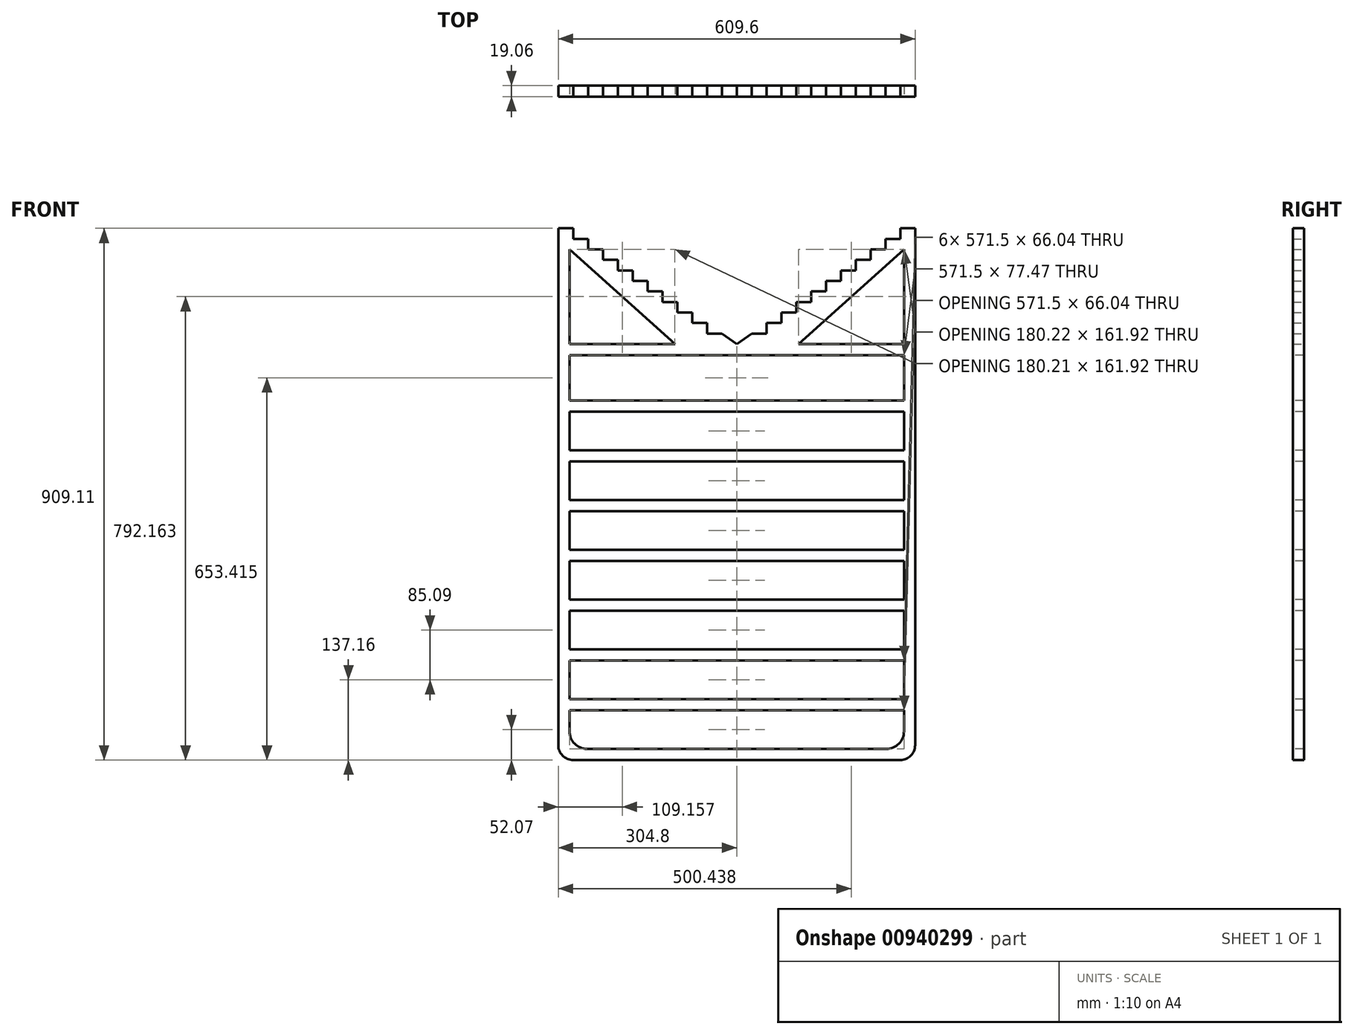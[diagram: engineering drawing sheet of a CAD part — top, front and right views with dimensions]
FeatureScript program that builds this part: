
annotation { "Feature Type Name" : "Feature", "Feature Type Description" : "" }
export const myFeature = defineFeature(function(context is Context, id is Id, definition is map)
    precondition{}
    {
        {
            var Q0;
            Q0=qCreatedBy(makeId("Front.planeOp"),FACE);
            var sketch = newSketch(context, id + "F0", { "sketchPlane" : qUnion([Q0])});
            skLineSegment(sketch, "E0.bottom", {"start": v(-304.8, -355.6) * mm, "end": v(304.8, -355.6) * mm});
            skLineSegment(sketch, "E0.top", {"start": v(-304.8, 355.6) * mm, "end": v(304.8, 355.6) * mm});
            skLineSegment(sketch, "E0.left", {"start": v(-304.8, -355.6) * mm, "end": v(-304.8, 355.6) * mm});
            skLineSegment(sketch, "E0.right", {"start": v(304.8, -355.6) * mm, "end": v(304.8, 355.6) * mm});
            skPoint(sketch, "E0.middle", {"position": v(0, 0) * mm});
            skLineSegment(sketch, "E1", {"start": v(-304.8, 355.6) * mm, "end": v(-304.8, 571.5) * mm});
            skLineSegment(sketch, "E2", {"start": v(304.8, 355.6) * mm, "end": v(304.8, 571.5) * mm});
            skLineSegment(sketch, "E3", {"start": v(304.8, 571.5) * mm, "end": v(304.8, 571.5) * mm});
            skLineSegment(sketch, "E4", {"start": v(304.8, 571.5) * mm, "end": v(0, 355.6) * mm});
            skLineSegment(sketch, "E5", {"start": v(0, 355.6) * mm, "end": v(-304.8, 571.5) * mm});
            skLineSegment(sketch, "E6", {"start": v(-304.8, 571.5) * mm, "end": v(-304.8, 571.5) * mm});
            skLineSegment(sketch, "E7.bottom", {"start": v(-279.4, 571.5) * mm, "end": v(-304.8, 571.5) * mm});
            skLineSegment(sketch, "E7.top", {"start": v(-279.4, 553.5) * mm, "end": v(-304.8, 553.5) * mm});
            skLineSegment(sketch, "E7.left", {"start": v(-279.4, 571.5) * mm, "end": v(-279.4, 553.5) * mm});
            skLineSegment(sketch, "E7.right", {"start": v(-304.8, 571.5) * mm, "end": v(-304.8, 553.5) * mm});
            skPoint(sketch, "E7.middle", {"position": v(-292.1, 562.5) * mm});
            skLineSegment(sketch, "E8.bottom", {"start": v(279.4, 571.5) * mm, "end": v(304.8, 571.5) * mm});
            skLineSegment(sketch, "E8.top", {"start": v(279.4, 553.5) * mm, "end": v(304.8, 553.5) * mm});
            skLineSegment(sketch, "E8.left", {"start": v(279.4, 571.5) * mm, "end": v(279.4, 553.5) * mm});
            skLineSegment(sketch, "E8.right", {"start": v(304.8, 571.5) * mm, "end": v(304.8, 553.5) * mm});
            skPoint(sketch, "E8.middle", {"position": v(292.1, 562.5) * mm});
            skLineSegment(sketch, "E9.bottom", {"start": v(-279.4, 553.5) * mm, "end": v(-254, 553.5) * mm});
            skLineSegment(sketch, "E9.top", {"start": v(-279.4, 535.52) * mm, "end": v(-254, 535.52) * mm});
            skLineSegment(sketch, "E9.left", {"start": v(-279.4, 553.5) * mm, "end": v(-279.4, 535.52) * mm});
            skLineSegment(sketch, "E9.right", {"start": v(-254, 553.5) * mm, "end": v(-254, 535.52) * mm});
            skLineSegment(sketch, "E10.bottom", {"start": v(-254, 535.52) * mm, "end": v(-228.6, 535.52) * mm});
            skLineSegment(sketch, "E10.top", {"start": v(-254, 517.52) * mm, "end": v(-228.6, 517.52) * mm});
            skLineSegment(sketch, "E10.left", {"start": v(-254, 535.52) * mm, "end": v(-254, 517.52) * mm});
            skLineSegment(sketch, "E10.right", {"start": v(-228.6, 535.52) * mm, "end": v(-228.6, 517.52) * mm});
            skLineSegment(sketch, "E11.bottom", {"start": v(-228.6, 517.52) * mm, "end": v(-203.2, 517.52) * mm});
            skLineSegment(sketch, "E11.top", {"start": v(-228.6, 499.53) * mm, "end": v(-203.2, 499.53) * mm});
            skLineSegment(sketch, "E11.left", {"start": v(-228.6, 517.52) * mm, "end": v(-228.6, 499.53) * mm});
            skLineSegment(sketch, "E11.right", {"start": v(-203.2, 517.52) * mm, "end": v(-203.2, 499.53) * mm});
            skLineSegment(sketch, "E12.bottom", {"start": v(-203.2, 499.53) * mm, "end": v(-177.8, 499.53) * mm});
            skLineSegment(sketch, "E12.top", {"start": v(-203.2, 481.54) * mm, "end": v(-177.8, 481.54) * mm});
            skLineSegment(sketch, "E12.left", {"start": v(-203.2, 499.53) * mm, "end": v(-203.2, 481.54) * mm});
            skLineSegment(sketch, "E12.right", {"start": v(-177.8, 499.53) * mm, "end": v(-177.8, 481.54) * mm});
            skLineSegment(sketch, "E13.bottom", {"start": v(279.4, 553.5) * mm, "end": v(254, 553.5) * mm});
            skLineSegment(sketch, "E13.top", {"start": v(279.4, 535.52) * mm, "end": v(254, 535.52) * mm});
            skLineSegment(sketch, "E13.left", {"start": v(279.4, 553.5) * mm, "end": v(279.4, 535.52) * mm});
            skLineSegment(sketch, "E13.right", {"start": v(254, 553.5) * mm, "end": v(254, 535.52) * mm});
            skLineSegment(sketch, "E14.bottom", {"start": v(254, 535.52) * mm, "end": v(228.6, 535.52) * mm});
            skLineSegment(sketch, "E14.top", {"start": v(254, 517.52) * mm, "end": v(228.6, 517.52) * mm});
            skLineSegment(sketch, "E14.left", {"start": v(254, 535.52) * mm, "end": v(254, 517.52) * mm});
            skLineSegment(sketch, "E14.right", {"start": v(228.6, 535.52) * mm, "end": v(228.6, 517.52) * mm});
            skLineSegment(sketch, "E15.bottom", {"start": v(-177.8, 481.54) * mm, "end": v(-152.4, 481.54) * mm});
            skLineSegment(sketch, "E15.top", {"start": v(-177.8, 463.55) * mm, "end": v(-152.4, 463.55) * mm});
            skLineSegment(sketch, "E15.left", {"start": v(-177.8, 481.54) * mm, "end": v(-177.8, 463.55) * mm});
            skLineSegment(sketch, "E15.right", {"start": v(-152.4, 481.54) * mm, "end": v(-152.4, 463.55) * mm});
            skLineSegment(sketch, "E16.bottom", {"start": v(-152.4, 463.55) * mm, "end": v(-127, 463.55) * mm});
            skLineSegment(sketch, "E16.top", {"start": v(-152.4, 445.56) * mm, "end": v(-127, 445.56) * mm});
            skLineSegment(sketch, "E16.left", {"start": v(-152.4, 463.55) * mm, "end": v(-152.4, 445.56) * mm});
            skLineSegment(sketch, "E16.right", {"start": v(-127, 463.55) * mm, "end": v(-127, 445.56) * mm});
            skLineSegment(sketch, "E17.bottom", {"start": v(-127, 445.56) * mm, "end": v(-101.6, 445.56) * mm});
            skLineSegment(sketch, "E17.top", {"start": v(-127, 427.57) * mm, "end": v(-101.6, 427.57) * mm});
            skLineSegment(sketch, "E17.left", {"start": v(-127, 445.56) * mm, "end": v(-127, 427.57) * mm});
            skLineSegment(sketch, "E17.right", {"start": v(-101.6, 445.56) * mm, "end": v(-101.6, 427.57) * mm});
            skLineSegment(sketch, "E18.bottom", {"start": v(-101.6, 427.57) * mm, "end": v(-76.2, 427.57) * mm});
            skLineSegment(sketch, "E18.top", {"start": v(-101.6, 409.57) * mm, "end": v(-76.2, 409.57) * mm});
            skLineSegment(sketch, "E18.left", {"start": v(-101.6, 427.57) * mm, "end": v(-101.6, 409.57) * mm});
            skLineSegment(sketch, "E18.right", {"start": v(-76.2, 427.57) * mm, "end": v(-76.2, 409.57) * mm});
            skLineSegment(sketch, "E19.bottom", {"start": v(-76.2, 409.57) * mm, "end": v(-50.8, 409.57) * mm});
            skLineSegment(sketch, "E19.top", {"start": v(-76.2, 391.58) * mm, "end": v(-50.8, 391.58) * mm});
            skLineSegment(sketch, "E19.left", {"start": v(-76.2, 409.57) * mm, "end": v(-76.2, 391.58) * mm});
            skLineSegment(sketch, "E19.right", {"start": v(-50.8, 409.57) * mm, "end": v(-50.8, 391.58) * mm});
            skLineSegment(sketch, "E20.bottom", {"start": v(-50.8, 391.58) * mm, "end": v(-25.4, 391.58) * mm});
            skLineSegment(sketch, "E20.top", {"start": v(-50.8, 373.6) * mm, "end": v(-25.4, 373.6) * mm});
            skLineSegment(sketch, "E20.left", {"start": v(-50.8, 391.58) * mm, "end": v(-50.8, 373.6) * mm});
            skLineSegment(sketch, "E20.right", {"start": v(-25.4, 391.58) * mm, "end": v(-25.4, 373.6) * mm});
            skPoint(sketch, "E21.right.start.orphan", {"position": v(203.2, 499.53) * mm});
            skPoint(sketch, "E22.top.end.orphan", {"position": v(177.8, 481.54) * mm});
            skLineSegment(sketch, "E23.bottom", {"start": v(228.6, 517.52) * mm, "end": v(203.2, 517.52) * mm});
            skLineSegment(sketch, "E23.top", {"start": v(228.6, 499.53) * mm, "end": v(203.2, 499.53) * mm});
            skLineSegment(sketch, "E23.left", {"start": v(228.6, 517.52) * mm, "end": v(228.6, 499.53) * mm});
            skLineSegment(sketch, "E23.right", {"start": v(203.2, 517.52) * mm, "end": v(203.2, 499.53) * mm});
            skLineSegment(sketch, "E24.bottom", {"start": v(203.2, 499.53) * mm, "end": v(177.8, 499.53) * mm});
            skLineSegment(sketch, "E24.top", {"start": v(203.2, 481.54) * mm, "end": v(177.8, 481.54) * mm});
            skLineSegment(sketch, "E24.left", {"start": v(203.2, 499.53) * mm, "end": v(203.2, 481.54) * mm});
            skLineSegment(sketch, "E24.right", {"start": v(177.8, 499.53) * mm, "end": v(177.8, 481.54) * mm});
            skLineSegment(sketch, "E25.bottom", {"start": v(177.8, 481.54) * mm, "end": v(152.4, 481.54) * mm});
            skLineSegment(sketch, "E25.top", {"start": v(177.8, 463.55) * mm, "end": v(152.4, 463.55) * mm});
            skLineSegment(sketch, "E25.left", {"start": v(177.8, 481.54) * mm, "end": v(177.8, 463.55) * mm});
            skLineSegment(sketch, "E25.right", {"start": v(152.4, 481.54) * mm, "end": v(152.4, 463.55) * mm});
            skLineSegment(sketch, "E26.bottom", {"start": v(152.4, 463.55) * mm, "end": v(127, 463.55) * mm});
            skLineSegment(sketch, "E26.top", {"start": v(152.4, 445.56) * mm, "end": v(127, 445.56) * mm});
            skLineSegment(sketch, "E26.left", {"start": v(152.4, 463.55) * mm, "end": v(152.4, 445.56) * mm});
            skLineSegment(sketch, "E26.right", {"start": v(127, 463.55) * mm, "end": v(127, 445.56) * mm});
            skLineSegment(sketch, "E27.bottom", {"start": v(127, 445.56) * mm, "end": v(101.6, 445.56) * mm});
            skLineSegment(sketch, "E27.top", {"start": v(127, 427.57) * mm, "end": v(101.6, 427.57) * mm});
            skLineSegment(sketch, "E27.left", {"start": v(127, 445.56) * mm, "end": v(127, 427.57) * mm});
            skLineSegment(sketch, "E27.right", {"start": v(101.6, 445.56) * mm, "end": v(101.6, 427.57) * mm});
            skLineSegment(sketch, "E28.bottom", {"start": v(101.6, 427.57) * mm, "end": v(76.2, 427.57) * mm});
            skLineSegment(sketch, "E28.top", {"start": v(101.6, 409.57) * mm, "end": v(76.2, 409.57) * mm});
            skLineSegment(sketch, "E28.left", {"start": v(101.6, 427.57) * mm, "end": v(101.6, 409.57) * mm});
            skLineSegment(sketch, "E28.right", {"start": v(76.2, 427.57) * mm, "end": v(76.2, 409.57) * mm});
            skLineSegment(sketch, "E29.bottom", {"start": v(76.2, 409.57) * mm, "end": v(50.8, 409.57) * mm});
            skLineSegment(sketch, "E29.top", {"start": v(76.2, 391.58) * mm, "end": v(50.8, 391.58) * mm});
            skLineSegment(sketch, "E29.left", {"start": v(76.2, 409.57) * mm, "end": v(76.2, 391.58) * mm});
            skLineSegment(sketch, "E29.right", {"start": v(50.8, 409.57) * mm, "end": v(50.8, 391.58) * mm});
            skLineSegment(sketch, "E30.bottom", {"start": v(50.8, 391.58) * mm, "end": v(25.4, 391.58) * mm});
            skLineSegment(sketch, "E30.top", {"start": v(50.8, 373.6) * mm, "end": v(25.4, 373.6) * mm});
            skLineSegment(sketch, "E30.left", {"start": v(50.8, 391.58) * mm, "end": v(50.8, 373.6) * mm});
            skLineSegment(sketch, "E30.right", {"start": v(25.4, 391.58) * mm, "end": v(25.4, 373.6) * mm});
            skSolve(sketch);
        }
        {
            var Q0;
            Q0=makeQuery(id+"F0.imprint","IMPRINT",FACE,{"disambiguationData":[TD([[makeQuery(id+"F0.imprint","IMPRINT",EDGE,{"derivedFrom":sQuery(id+"F0.wireOp",EDGE,"E0.bottom")}),1.0]])]});
            var Q1;
            {var subQ0=sQuery(id+"F0.wireOp",EDGE,"E7.top");Q1=makeQuery(id+"F0.imprint","IMPRINT",FACE,{"disambiguationData":[TD([[makeQuery(id+"F0.imprint","IMPRINT",EDGE,{"derivedFrom":subQ0}),1.0]])]});}
            var Q2;
            {var subQ3=sQuery(id+"F0.wireOp",EDGE,"E8.top");Q2=makeQuery(id+"F0.imprint","IMPRINT",FACE,{"disambiguationData":[TD([[makeQuery(id+"F0.imprint","IMPRINT",EDGE,{"derivedFrom":subQ3}),-1.0]])]});}
            extrude(context, id + "F1", {"entities" : qUnion([Q0, Q1, Q2]), "endBound" : BoundingType.SYMMETRIC, "depth" : 19.05 * mm, "offsetDistance" : 25.4 * mm});
        }
        {
            var Q0;
            Q0=makeQuery(id+"F1.opExtrude","SWEPT_EDGE",EDGE,{"disambiguationData":[OSD([sQuery(id+"F0.wireOp",EDGE,"E0.bottom"),sQuery(id+"F0.wireOp",EDGE,"E0.left")])]});
            var Q1;
            Q1=makeQuery(id+"F1.opExtrude","SWEPT_EDGE",EDGE,{"disambiguationData":[OSD([sQuery(id+"F0.wireOp",EDGE,"E0.bottom"),sQuery(id+"F0.wireOp",EDGE,"E0.right")])]});
            fillet(context, id + "F2", {"entities" : qUnion([Q0, Q1]), "radius" : 25.4 * mm, "tangentPropagation" : true, "allowEdgeOverflow" : false});
        }
        {
            var Q0;
            Q0=makeQuery(id+"F1.opExtrude","CAP_FACE",FACE,{"disambiguationData":[OSD([sQuery(id+"F0.wireOp",EDGE,"E0.bottom"),sQuery(id+"F0.wireOp",EDGE,"E0.left"),sQuery(id+"F0.wireOp",EDGE,"E0.right"),sQuery(id+"F0.wireOp",EDGE,"E1"),sQuery(id+"F0.wireOp",EDGE,"E2"),sQuery(id+"F0.wireOp",EDGE,"E4"),sQuery(id+"F0.wireOp",EDGE,"E5"),sQuery(id+"F0.wireOp",EDGE,"E7.top"),sQuery(id+"F0.wireOp",EDGE,"E8.top"),sQuery(id+"F0.wireOp",EDGE,"E9.top"),sQuery(id+"F0.wireOp",EDGE,"E9.left"),sQuery(id+"F0.wireOp",EDGE,"E10.top"),sQuery(id+"F0.wireOp",EDGE,"E10.left"),sQuery(id+"F0.wireOp",EDGE,"E11.top"),sQuery(id+"F0.wireOp",EDGE,"E11.left"),sQuery(id+"F0.wireOp",EDGE,"E12.top"),sQuery(id+"F0.wireOp",EDGE,"E12.left"),sQuery(id+"F0.wireOp",EDGE,"E13.top"),sQuery(id+"F0.wireOp",EDGE,"E13.left"),sQuery(id+"F0.wireOp",EDGE,"E14.top"),sQuery(id+"F0.wireOp",EDGE,"E14.left"),sQuery(id+"F0.wireOp",EDGE,"E15.top"),sQuery(id+"F0.wireOp",EDGE,"E15.left"),sQuery(id+"F0.wireOp",EDGE,"E16.top"),sQuery(id+"F0.wireOp",EDGE,"E16.left"),sQuery(id+"F0.wireOp",EDGE,"E17.top"),sQuery(id+"F0.wireOp",EDGE,"E17.left"),sQuery(id+"F0.wireOp",EDGE,"E18.top"),sQuery(id+"F0.wireOp",EDGE,"E18.left"),sQuery(id+"F0.wireOp",EDGE,"E19.top"),sQuery(id+"F0.wireOp",EDGE,"E19.left"),sQuery(id+"F0.wireOp",EDGE,"E20.top"),sQuery(id+"F0.wireOp",EDGE,"E20.left"),sQuery(id+"F0.wireOp",EDGE,"E23.top"),sQuery(id+"F0.wireOp",EDGE,"E23.left"),sQuery(id+"F0.wireOp",EDGE,"E24.top"),sQuery(id+"F0.wireOp",EDGE,"E24.left"),sQuery(id+"F0.wireOp",EDGE,"E25.top"),sQuery(id+"F0.wireOp",EDGE,"E25.left"),sQuery(id+"F0.wireOp",EDGE,"E26.top"),sQuery(id+"F0.wireOp",EDGE,"E26.left"),sQuery(id+"F0.wireOp",EDGE,"E27.top"),sQuery(id+"F0.wireOp",EDGE,"E27.left"),sQuery(id+"F0.wireOp",EDGE,"E28.top"),sQuery(id+"F0.wireOp",EDGE,"E28.left"),sQuery(id+"F0.wireOp",EDGE,"E29.top"),sQuery(id+"F0.wireOp",EDGE,"E29.left"),sQuery(id+"F0.wireOp",EDGE,"E30.top"),sQuery(id+"F0.wireOp",EDGE,"E30.left")])],"isStart":false});
            var sketch = newSketch(context, id + "F3", { "sketchPlane" : qUnion([Q0])});
            skLineSegment(sketch, "E31.bottom", {"start": v(-285.75, -336.55) * mm, "end": v(285.75, -336.55) * mm});
            skLineSegment(sketch, "E31.top", {"start": v(-285.75, 336.55) * mm, "end": v(285.75, 336.55) * mm});
            skLineSegment(sketch, "E31.left", {"start": v(-285.75, -336.55) * mm, "end": v(-285.75, 336.55) * mm});
            skLineSegment(sketch, "E31.right", {"start": v(285.75, -336.55) * mm, "end": v(285.75, 336.55) * mm});
            skPoint(sketch, "E31.middle", {"position": v(0, 0) * mm});
            skSolve(sketch);
        }
        {
            var Q0;
            Q0 = qSketchRegion(id + "F3", true);
            extrude(context, id + "F4", {"entities" : qUnion([Q0]), "operationType" : NewBodyOperationType.REMOVE, "endBound" : BoundingType.THROUGH_ALL, "oppositeDirection" : true, "depth" : 25.4 * mm, "offsetDistance" : 25.4 * mm});
        }
        {
            var Q0;
            Q0=makeQuery(id+"F4.boolean.opBoolean","COPY",EDGE,{"derivedFrom":makeQuery(id+"F4.opExtrude","SWEPT_EDGE",EDGE,{"disambiguationData":[OSD([sQuery(id+"F3.wireOp",EDGE,"E31.bottom"),sQuery(id+"F3.wireOp",EDGE,"E31.right")])]})});
            var Q1;
            Q1=makeQuery(id+"F4.boolean.opBoolean","COPY",EDGE,{"derivedFrom":makeQuery(id+"F4.opExtrude","SWEPT_EDGE",EDGE,{"disambiguationData":[OSD([sQuery(id+"F3.wireOp",EDGE,"E31.bottom"),sQuery(id+"F3.wireOp",EDGE,"E31.left")])]})});
            fillet(context, id + "F5", {"entities" : qUnion([Q0, Q1]), "radius" : 30.1 * mm, "tangentPropagation" : true, "allowEdgeOverflow" : false});
        }
        {
            var Q0;
            Q0=makeQuery(id+"F1.opExtrude","CAP_FACE",FACE,{"disambiguationData":[OSD([sQuery(id+"F0.wireOp",EDGE,"E0.bottom"),sQuery(id+"F0.wireOp",EDGE,"E0.left"),sQuery(id+"F0.wireOp",EDGE,"E0.right"),sQuery(id+"F0.wireOp",EDGE,"E1"),sQuery(id+"F0.wireOp",EDGE,"E2"),sQuery(id+"F0.wireOp",EDGE,"E4"),sQuery(id+"F0.wireOp",EDGE,"E5"),sQuery(id+"F0.wireOp",EDGE,"E7.top"),sQuery(id+"F0.wireOp",EDGE,"E8.top"),sQuery(id+"F0.wireOp",EDGE,"E9.top"),sQuery(id+"F0.wireOp",EDGE,"E9.left"),sQuery(id+"F0.wireOp",EDGE,"E10.top"),sQuery(id+"F0.wireOp",EDGE,"E10.left"),sQuery(id+"F0.wireOp",EDGE,"E11.top"),sQuery(id+"F0.wireOp",EDGE,"E11.left"),sQuery(id+"F0.wireOp",EDGE,"E12.top"),sQuery(id+"F0.wireOp",EDGE,"E12.left"),sQuery(id+"F0.wireOp",EDGE,"E13.top"),sQuery(id+"F0.wireOp",EDGE,"E13.left"),sQuery(id+"F0.wireOp",EDGE,"E14.top"),sQuery(id+"F0.wireOp",EDGE,"E14.left"),sQuery(id+"F0.wireOp",EDGE,"E15.top"),sQuery(id+"F0.wireOp",EDGE,"E15.left"),sQuery(id+"F0.wireOp",EDGE,"E16.top"),sQuery(id+"F0.wireOp",EDGE,"E16.left"),sQuery(id+"F0.wireOp",EDGE,"E17.top"),sQuery(id+"F0.wireOp",EDGE,"E17.left"),sQuery(id+"F0.wireOp",EDGE,"E18.top"),sQuery(id+"F0.wireOp",EDGE,"E18.left"),sQuery(id+"F0.wireOp",EDGE,"E19.top"),sQuery(id+"F0.wireOp",EDGE,"E19.left"),sQuery(id+"F0.wireOp",EDGE,"E20.top"),sQuery(id+"F0.wireOp",EDGE,"E20.left"),sQuery(id+"F0.wireOp",EDGE,"E23.top"),sQuery(id+"F0.wireOp",EDGE,"E23.left"),sQuery(id+"F0.wireOp",EDGE,"E24.top"),sQuery(id+"F0.wireOp",EDGE,"E24.left"),sQuery(id+"F0.wireOp",EDGE,"E25.top"),sQuery(id+"F0.wireOp",EDGE,"E25.left"),sQuery(id+"F0.wireOp",EDGE,"E26.top"),sQuery(id+"F0.wireOp",EDGE,"E26.left"),sQuery(id+"F0.wireOp",EDGE,"E27.top"),sQuery(id+"F0.wireOp",EDGE,"E27.left"),sQuery(id+"F0.wireOp",EDGE,"E28.top"),sQuery(id+"F0.wireOp",EDGE,"E28.left"),sQuery(id+"F0.wireOp",EDGE,"E29.top"),sQuery(id+"F0.wireOp",EDGE,"E29.left"),sQuery(id+"F0.wireOp",EDGE,"E30.top"),sQuery(id+"F0.wireOp",EDGE,"E30.left")])],"isStart":false});
            var sketch = newSketch(context, id + "F6", { "sketchPlane" : qUnion([Q0])});
            skLineSegment(sketch, "E32", {"start": v(-105.54, 355.6) * mm, "end": v(-285.75, 355.6) * mm});
            skLineSegment(sketch, "E33", {"start": v(-285.75, 355.6) * mm, "end": v(-285.75, 517.52) * mm});
            skLineSegment(sketch, "E34", {"start": v(-285.75, 517.52) * mm, "end": v(-105.54, 355.6) * mm});
            skLineSegment(sketch, "E35", {"start": v(285.75, 355.6) * mm, "end": v(105.53, 355.6) * mm});
            skLineSegment(sketch, "E36", {"start": v(105.53, 355.6) * mm, "end": v(285.75, 517.52) * mm});
            skLineSegment(sketch, "E37", {"start": v(285.75, 517.52) * mm, "end": v(285.75, 355.6) * mm});
            skSolve(sketch);
        }
        {
            var Q0;
            Q0=makeQuery(id+"F6.imprint","IMPRINT",FACE,{"disambiguationData":[TD([[makeQuery(id+"F6.imprint","IMPRINT",EDGE,{"derivedFrom":sQuery(id+"F6.wireOp",EDGE,"E32")}),-1.0]])]});
            var Q1;
            Q1=makeQuery(id+"F6.imprint","IMPRINT",FACE,{"disambiguationData":[TD([[makeQuery(id+"F6.imprint","IMPRINT",EDGE,{"derivedFrom":sQuery(id+"F6.wireOp",EDGE,"E35")}),-1.0]])]});
            extrude(context, id + "F7", {"entities" : qUnion([Q0, Q1]), "operationType" : NewBodyOperationType.REMOVE, "endBound" : BoundingType.THROUGH_ALL, "oppositeDirection" : true, "depth" : 25.4 * mm, "offsetDistance" : 25.4 * mm});
        }
        {
            var Q0;
            Q0=makeQuery(id+"F1.opExtrude","CAP_FACE",FACE,{"disambiguationData":[OSD([sQuery(id+"F0.wireOp",EDGE,"E0.bottom"),sQuery(id+"F0.wireOp",EDGE,"E0.left"),sQuery(id+"F0.wireOp",EDGE,"E0.right"),sQuery(id+"F0.wireOp",EDGE,"E1"),sQuery(id+"F0.wireOp",EDGE,"E2"),sQuery(id+"F0.wireOp",EDGE,"E4"),sQuery(id+"F0.wireOp",EDGE,"E5"),sQuery(id+"F0.wireOp",EDGE,"E7.top"),sQuery(id+"F0.wireOp",EDGE,"E8.top"),sQuery(id+"F0.wireOp",EDGE,"E9.top"),sQuery(id+"F0.wireOp",EDGE,"E9.left"),sQuery(id+"F0.wireOp",EDGE,"E10.top"),sQuery(id+"F0.wireOp",EDGE,"E10.left"),sQuery(id+"F0.wireOp",EDGE,"E11.top"),sQuery(id+"F0.wireOp",EDGE,"E11.left"),sQuery(id+"F0.wireOp",EDGE,"E12.top"),sQuery(id+"F0.wireOp",EDGE,"E12.left"),sQuery(id+"F0.wireOp",EDGE,"E13.top"),sQuery(id+"F0.wireOp",EDGE,"E13.left"),sQuery(id+"F0.wireOp",EDGE,"E14.top"),sQuery(id+"F0.wireOp",EDGE,"E14.left"),sQuery(id+"F0.wireOp",EDGE,"E15.top"),sQuery(id+"F0.wireOp",EDGE,"E15.left"),sQuery(id+"F0.wireOp",EDGE,"E16.top"),sQuery(id+"F0.wireOp",EDGE,"E16.left"),sQuery(id+"F0.wireOp",EDGE,"E17.top"),sQuery(id+"F0.wireOp",EDGE,"E17.left"),sQuery(id+"F0.wireOp",EDGE,"E18.top"),sQuery(id+"F0.wireOp",EDGE,"E18.left"),sQuery(id+"F0.wireOp",EDGE,"E19.top"),sQuery(id+"F0.wireOp",EDGE,"E19.left"),sQuery(id+"F0.wireOp",EDGE,"E20.top"),sQuery(id+"F0.wireOp",EDGE,"E20.left"),sQuery(id+"F0.wireOp",EDGE,"E23.top"),sQuery(id+"F0.wireOp",EDGE,"E23.left"),sQuery(id+"F0.wireOp",EDGE,"E24.top"),sQuery(id+"F0.wireOp",EDGE,"E24.left"),sQuery(id+"F0.wireOp",EDGE,"E25.top"),sQuery(id+"F0.wireOp",EDGE,"E25.left"),sQuery(id+"F0.wireOp",EDGE,"E26.top"),sQuery(id+"F0.wireOp",EDGE,"E26.left"),sQuery(id+"F0.wireOp",EDGE,"E27.top"),sQuery(id+"F0.wireOp",EDGE,"E27.left"),sQuery(id+"F0.wireOp",EDGE,"E28.top"),sQuery(id+"F0.wireOp",EDGE,"E28.left"),sQuery(id+"F0.wireOp",EDGE,"E29.top"),sQuery(id+"F0.wireOp",EDGE,"E29.left"),sQuery(id+"F0.wireOp",EDGE,"E30.top"),sQuery(id+"F0.wireOp",EDGE,"E30.left")])],"isStart":false});
            var sketch = newSketch(context, id + "F8", { "sketchPlane" : qUnion([Q0])});
            skLineSegment(sketch, "E38.bottom", {"start": v(-285.75, 259.08) * mm, "end": v(285.75, 259.08) * mm});
            skLineSegment(sketch, "E38.top", {"start": v(-285.75, 240.03) * mm, "end": v(285.75, 240.03) * mm});
            skLineSegment(sketch, "E38.left", {"start": v(-285.75, 259.08) * mm, "end": v(-285.75, 240.03) * mm});
            skLineSegment(sketch, "E38.right", {"start": v(285.75, 259.08) * mm, "end": v(285.75, 240.03) * mm});
            skLineSegment(sketch, "E39.bottom", {"start": v(-285.75, 174) * mm, "end": v(285.75, 174) * mm});
            skLineSegment(sketch, "E39.top", {"start": v(-285.75, 154.94) * mm, "end": v(285.75, 154.94) * mm});
            skLineSegment(sketch, "E39.left", {"start": v(-285.75, 174) * mm, "end": v(-285.75, 154.94) * mm});
            skLineSegment(sketch, "E39.right", {"start": v(285.75, 174) * mm, "end": v(285.75, 154.94) * mm});
            skLineSegment(sketch, "E40.bottom", {"start": v(-285.75, 88.9) * mm, "end": v(285.75, 88.9) * mm});
            skLineSegment(sketch, "E40.top", {"start": v(-285.75, 69.85) * mm, "end": v(285.75, 69.85) * mm});
            skLineSegment(sketch, "E40.left", {"start": v(-285.75, 88.9) * mm, "end": v(-285.75, 69.85) * mm});
            skLineSegment(sketch, "E40.right", {"start": v(285.75, 88.9) * mm, "end": v(285.75, 69.85) * mm});
            skLineSegment(sketch, "E41.bottom", {"start": v(-285.75, -81.28) * mm, "end": v(285.75, -81.28) * mm});
            skLineSegment(sketch, "E41.top", {"start": v(-285.75, -100.33) * mm, "end": v(285.75, -100.33) * mm});
            skLineSegment(sketch, "E41.left", {"start": v(-285.75, -81.28) * mm, "end": v(-285.75, -100.33) * mm});
            skLineSegment(sketch, "E41.right", {"start": v(285.75, -81.28) * mm, "end": v(285.75, -100.33) * mm});
            skLineSegment(sketch, "E42.bottom", {"start": v(-285.75, -166.37) * mm, "end": v(285.75, -166.37) * mm});
            skLineSegment(sketch, "E42.top", {"start": v(-285.75, -185.42) * mm, "end": v(285.75, -185.42) * mm});
            skLineSegment(sketch, "E42.left", {"start": v(-285.75, -166.37) * mm, "end": v(-285.75, -185.42) * mm});
            skLineSegment(sketch, "E42.right", {"start": v(285.75, -166.37) * mm, "end": v(285.75, -185.42) * mm});
            skLineSegment(sketch, "E43.bottom", {"start": v(-285.75, 3.81) * mm, "end": v(285.75, 3.81) * mm});
            skLineSegment(sketch, "E43.top", {"start": v(-285.75, -15.24) * mm, "end": v(285.75, -15.24) * mm});
            skLineSegment(sketch, "E43.left", {"start": v(-285.75, 3.81) * mm, "end": v(-285.75, -15.24) * mm});
            skLineSegment(sketch, "E43.right", {"start": v(285.75, 3.81) * mm, "end": v(285.75, -15.24) * mm});
            skLineSegment(sketch, "E44.bottom", {"start": v(-285.75, -251.46) * mm, "end": v(285.75, -251.46) * mm});
            skLineSegment(sketch, "E44.top", {"start": v(-285.75, -270.5) * mm, "end": v(285.75, -270.5) * mm});
            skLineSegment(sketch, "E44.left", {"start": v(-285.75, -251.46) * mm, "end": v(-285.75, -270.5) * mm});
            skLineSegment(sketch, "E44.right", {"start": v(285.75, -251.46) * mm, "end": v(285.75, -270.5) * mm});
            skSolve(sketch);
        }
        {
            var Q0;
            Q0=makeQuery(id+"F8.imprint","IMPRINT",FACE,{"disambiguationData":[TD([[makeQuery(id+"F8.imprint","IMPRINT",EDGE,{"derivedFrom":sQuery(id+"F8.wireOp",EDGE,"E39.bottom")}),-1.0]])]});
            var Q1;
            Q1=makeQuery(id+"F8.imprint","IMPRINT",FACE,{"disambiguationData":[TD([[makeQuery(id+"F8.imprint","IMPRINT",EDGE,{"derivedFrom":sQuery(id+"F8.wireOp",EDGE,"E38.bottom")}),-1.0]])]});
            var Q2;
            Q2=makeQuery(id+"F8.imprint","IMPRINT",FACE,{"disambiguationData":[TD([[makeQuery(id+"F8.imprint","IMPRINT",EDGE,{"derivedFrom":sQuery(id+"F8.wireOp",EDGE,"E40.bottom")}),-1.0]])]});
            var Q3;
            Q3=makeQuery(id+"F8.imprint","IMPRINT",FACE,{"disambiguationData":[TD([[makeQuery(id+"F8.imprint","IMPRINT",EDGE,{"derivedFrom":sQuery(id+"F8.wireOp",EDGE,"E43.bottom")}),-1.0]])]});
            var Q4;
            Q4=makeQuery(id+"F8.imprint","IMPRINT",FACE,{"disambiguationData":[TD([[makeQuery(id+"F8.imprint","IMPRINT",EDGE,{"derivedFrom":sQuery(id+"F8.wireOp",EDGE,"E41.bottom")}),-1.0]])]});
            var Q5;
            Q5=makeQuery(id+"F8.imprint","IMPRINT",FACE,{"disambiguationData":[TD([[makeQuery(id+"F8.imprint","IMPRINT",EDGE,{"derivedFrom":sQuery(id+"F8.wireOp",EDGE,"E42.bottom")}),-1.0]])]});
            var Q6;
            Q6=makeQuery(id+"F8.imprint","IMPRINT",FACE,{"disambiguationData":[TD([[makeQuery(id+"F8.imprint","IMPRINT",EDGE,{"derivedFrom":sQuery(id+"F8.wireOp",EDGE,"E44.bottom")}),-1.0]])]});
            extrude(context, id + "F9", {"entities" : qUnion([Q0, Q1, Q2, Q3, Q4, Q5, Q6]), "operationType" : NewBodyOperationType.ADD, "oppositeDirection" : true, "depth" : 19.05 * mm, "offsetDistance" : 25.4 * mm});
        }
    });
